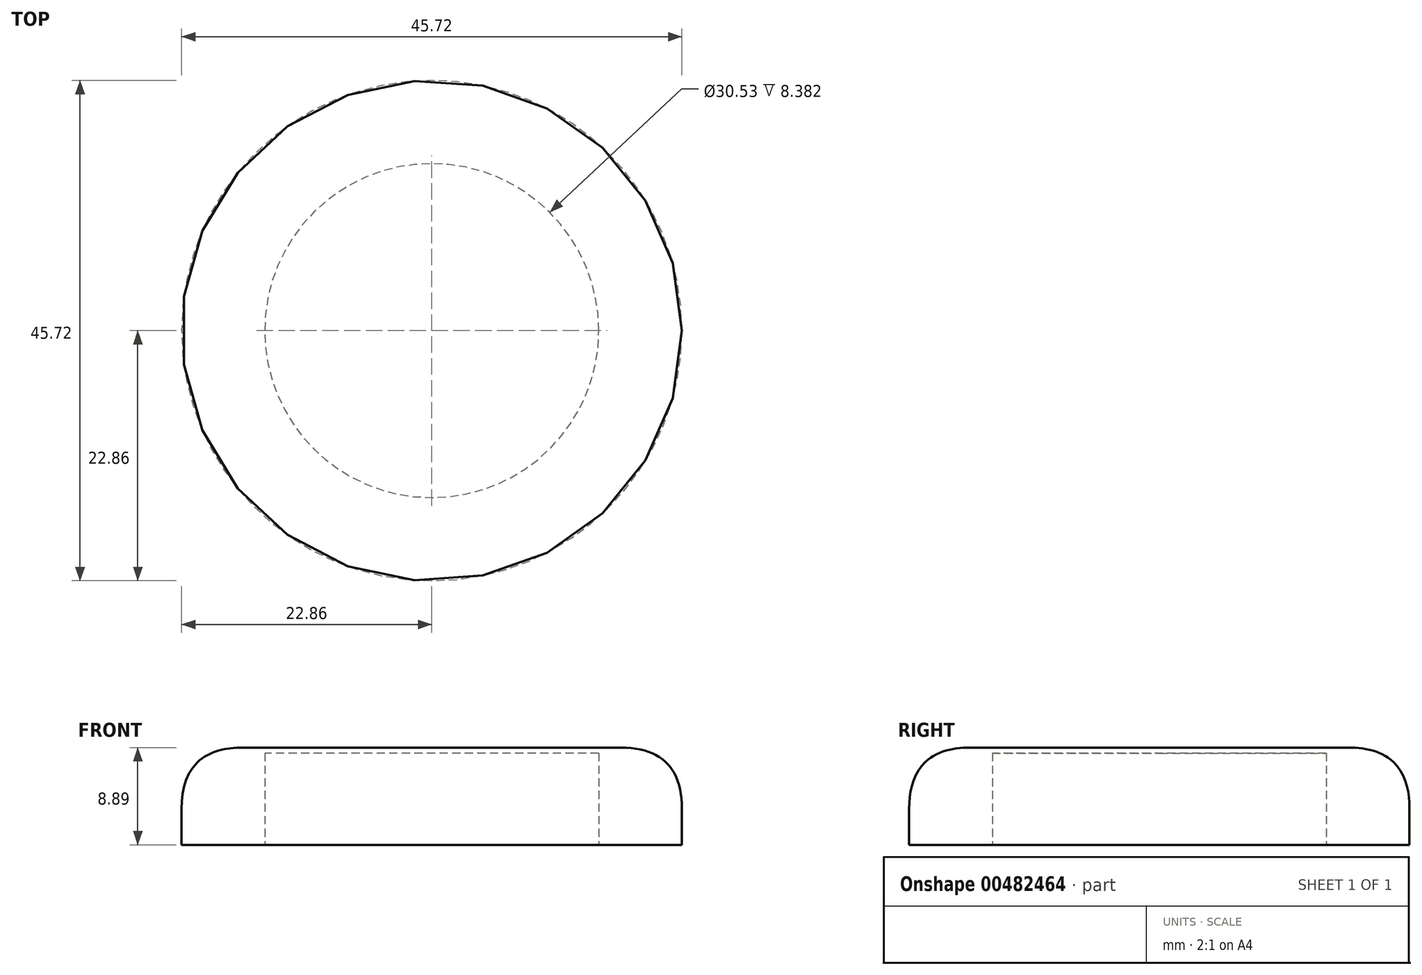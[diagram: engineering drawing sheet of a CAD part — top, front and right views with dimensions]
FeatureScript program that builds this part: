
annotation { "Feature Type Name" : "Feature", "Feature Type Description" : "" }
export const myFeature = defineFeature(function(context is Context, id is Id, definition is map)
    precondition{}
    {
        {
            var Q0;
            Q0=qCreatedBy(makeId("Top.planeOp"),FACE);
            var sketch = newSketch(context, id + "F0", { "sketchPlane" : qUnion([Q0])});
            skCircle(sketch, "E0", {"center": v(0, 0) * mm, "radius": 22.86 * mm});
            skSolve(sketch);
        }
        {
            var Q0;
            Q0 = qSketchRegion(id + "F0", true);
            extrude(context, id + "F1", {"entities" : qUnion([Q0]), "depth" : 8.9 * mm});
        }
        {
            var Q0;
            Q0=makeQuery(id+"F1.opExtrude","CAP_EDGE",EDGE,{"disambiguationData":[OSD([sQuery(id+"F0.wireOp",EDGE,"E0")])],"isStart":false});
            fillet(context, id + "F2", {"entities" : qUnion([Q0]), "radius" : 5.6 * mm, "tangentPropagation" : true, "rho" : 0.5, "crossSection" : FilletCrossSection.CONIC, "allowEdgeOverflow" : false});
        }
        {
            var Q0;
            Q0=qCreatedBy(makeId("Top.planeOp"),FACE);
            var sketch = newSketch(context, id + "F3", { "sketchPlane" : qUnion([Q0])});
            skCircle(sketch, "E1", {"center": v(0, 0) * mm, "radius": 15.26 * mm});
            skSolve(sketch);
        }
        {
            var Q0;
            Q0=makeQuery(id+"F3.imprint","IMPRINT",FACE,{"disambiguationData":[TD([[makeQuery(id+"F3.imprint","IMPRINT",EDGE,{"derivedFrom":sQuery(id+"F3.wireOp",EDGE,"E1")}),1.0]])]});
            extrude(context, id + "F4", {"entities" : qUnion([Q0]), "operationType" : NewBodyOperationType.REMOVE, "depth" : 8.38 * mm});
        }
    });
